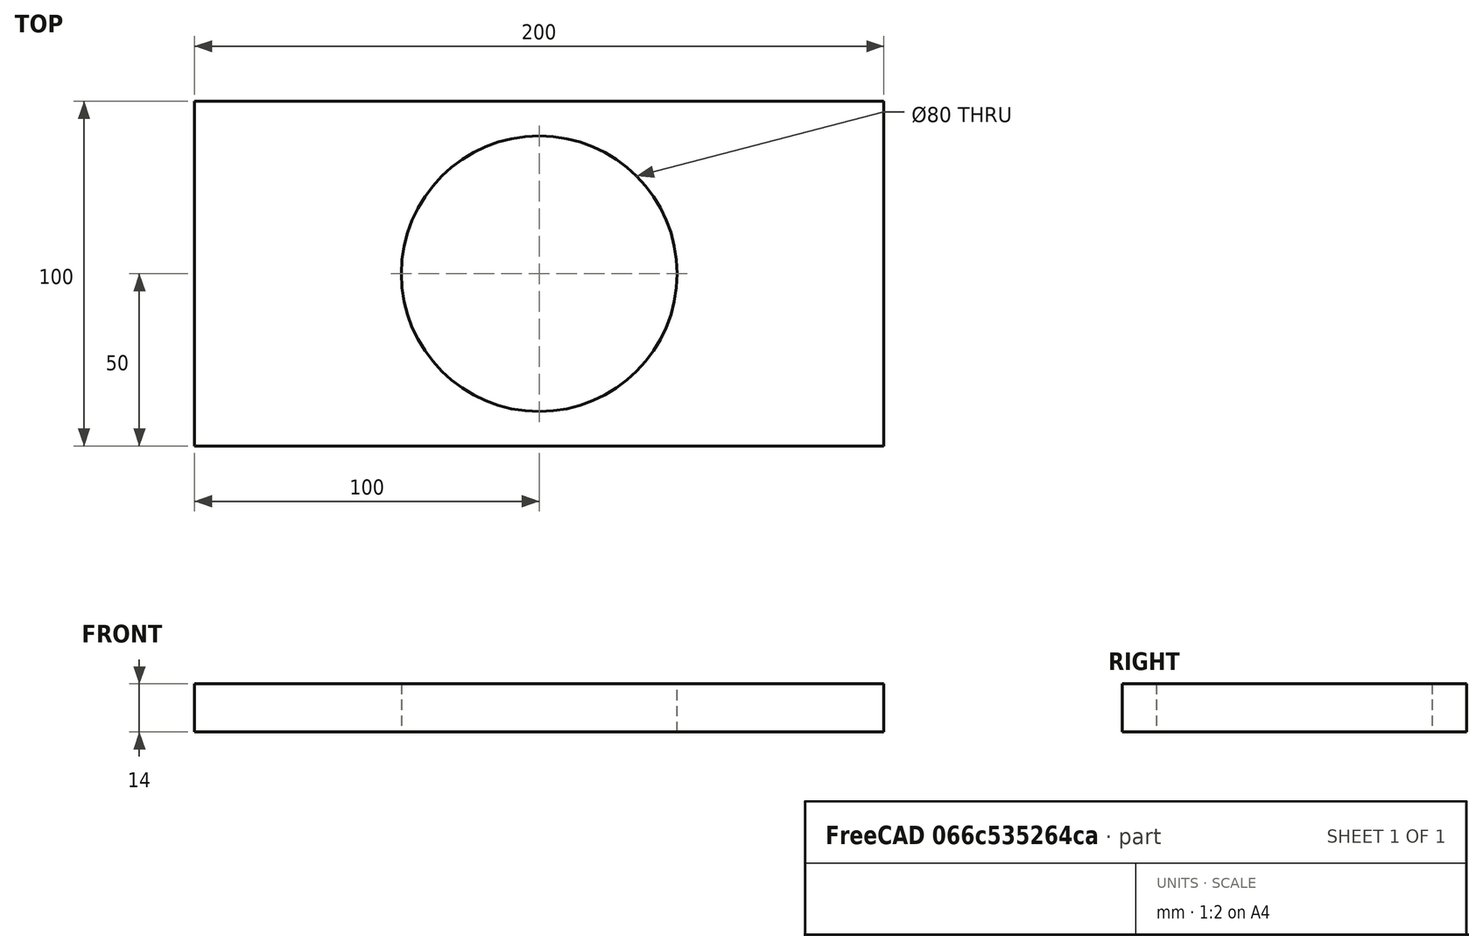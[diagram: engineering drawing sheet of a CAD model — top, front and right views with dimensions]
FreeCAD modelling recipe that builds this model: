
FCSTD DOCUMENT  (FreeCAD 0.19R24276 (Git))
Label: Plate_200x100_otv_d80
License: All rights reserved
LicenseURL: http://en.wikipedia.org/wiki/All_rights_reserved
objects: Sketcher::SketchObject×1, PartDesign::Pad×1, PartDesign::Body×1
note: 4 computed .brp shape members not serialized (recipe doc carries the construction recipe); baked Part::Feature solids carry a one-line shape summary decoded from their .brp

FEATURE [Sketcher::SketchObject] Sketch
  FullyConstrained = true
  MapMode = 5
  Support = -> [XY_Plane]
  sketch-geometry (5):
    g0: LineSegment StartX=0 StartY=0 StartZ=0 EndX=200 EndY=0 EndZ=0
    g1: LineSegment StartX=200 StartY=0 StartZ=0 EndX=200 EndY=100 EndZ=0
    g2: LineSegment StartX=200 StartY=100 StartZ=0 EndX=0 EndY=100 EndZ=0
    g3: LineSegment StartX=0 StartY=100 StartZ=0 EndX=0 EndY=0 EndZ=0
    g4: Circle CenterX=100 CenterY=50 CenterZ=0 NormalX=0 NormalY=0 NormalZ=1 AngleXU=0 Radius=40
  constraints (13):
    c: Coincident(g0,g1)
    c: Coincident(g1,g2)
    c: Coincident(g2,g3)
    c: Coincident(g3,g0)
    c: Horizontal(g0)
    c: Horizontal(g2)
    c: Vertical(g1)
    c: Vertical(g3)
    c: Coincident(g0,g-1)
    c: DistanceY(g1,g1) = 100
    c: DistanceX(g0,g0) = 200
    c: Symmetric(g0,g1,g4)
    c: Diameter(g4) = 80
FEATURE [PartDesign::Pad] Pad
  Direction = (1,1,1)
  Length = 14
  Length2 = 100
  Profile = -> Sketch
  Type = 0
FEATURE [PartDesign::Body] Body
  Group = -> [Sketch,Pad]
  Origin = -> Origin
  Tip = -> Pad
